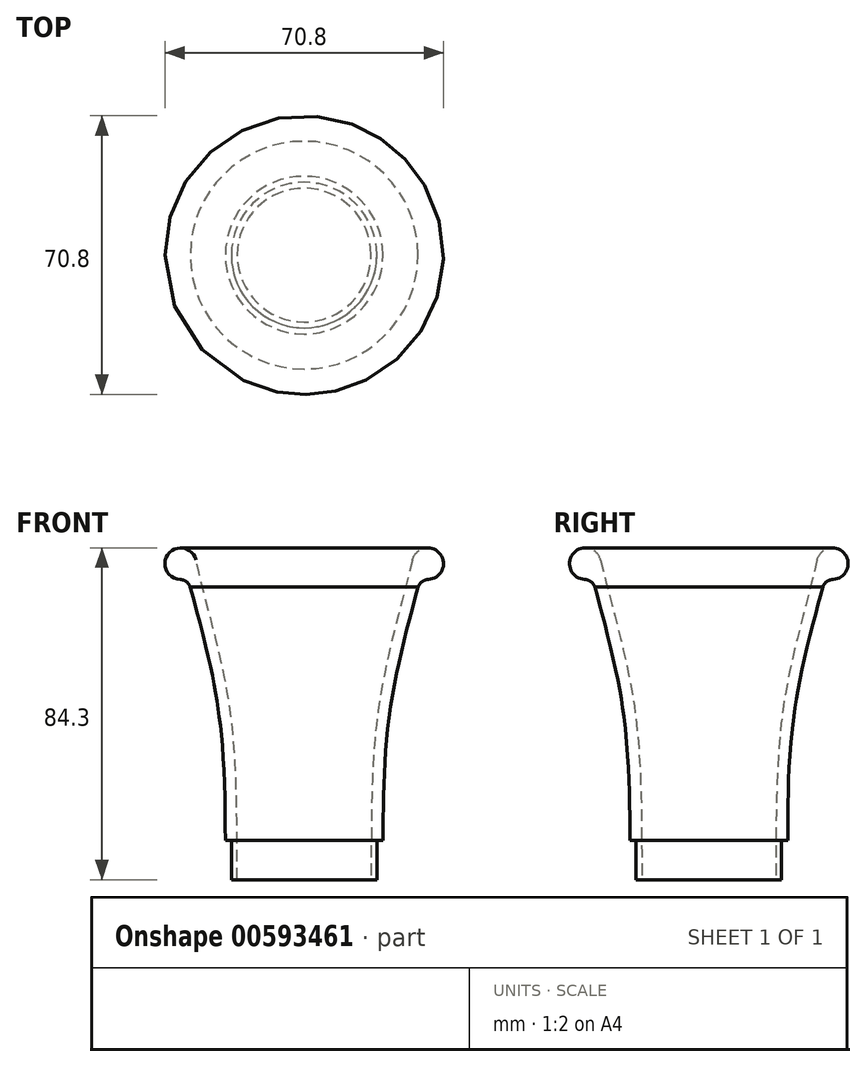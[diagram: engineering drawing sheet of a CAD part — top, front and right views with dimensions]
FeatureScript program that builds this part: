
annotation { "Feature Type Name" : "Feature", "Feature Type Description" : "" }
export const myFeature = defineFeature(function(context is Context, id is Id, definition is map)
    precondition{}
    {
        {
            var Q0;
            Q0=qCreatedBy(makeId("Right.planeOp"),FACE);
            var sketch = newSketch(context, id + "F0", { "sketchPlane" : qUnion([Q0])});
            skFitSpline(sketch, "E0", {"points": [v(-17, 0) * mm, v(-18.93, 44.07) * mm, v(-27.5, 81.2) * mm], "startDerivative": vector(-0.64, 86.47) * mm, "endDerivative": vector(-17.07, 73.05) * mm});
            skLineSegment(sketch, "E1", {"start": v(0, 0) * mm, "end": v(0, 81.2) * mm, "construction": true});
            skLineSegment(sketch, "E2", {"start": v(-27.5, 81.2) * mm, "end": v(0, 81.2) * mm, "construction": true});
            skLineSegment(sketch, "E3", {"start": v(-17, 0) * mm, "end": v(0, 0) * mm, "construction": true});
            skArc(sketch, "E4", {"start": v(-27.5, 81.2) * mm, "mid": v(-34.47, 82.86) * mm, "end": v(-31.59, 76.3) * mm});
            skFitSpline(sketch, "E5.0", {"points": [v(-20, -0.02) * mm, v(-20.03, 3.6) * mm, v(-20.04, 10.81) * mm, v(-20.16, 21.52) * mm, v(-20.53, 30.28) * mm, v(-21.09, 37.13) * mm, v(-21.57, 41.35) * mm, v(-22.05, 44.67) * mm, v(-22.6, 47.97) * mm, v(-23.38, 52.06) * mm, v(-24.46, 56.92) * mm, v(-26.02, 63.33) * mm, v(-28.1, 71.22) * mm, v(-29.7, 77.44) * mm, v(-30.42, 80.52) * mm]});
            skPoint(sketch, "E6.visualSharp", {"position": v(-29.51, 76.77) * mm});
            skArc(sketch, "E6.filletArc", {"start": v(-28.83, 74.05) * mm, "mid": v(-29.84, 75.63) * mm, "end": v(-31.59, 76.3) * mm});
            skLineSegment(sketch, "E7", {"start": v(-20, -0.02) * mm, "end": v(-17, 0) * mm});
            skSolve(sketch);
        }
        {
            var Q0;
            Q0 = qSketchRegion(id + "F0", true);
            var Q1;
            Q1=sQuery(id+"F0.wireOp",EDGE,"E1");
            revolve(context, id + "F1", {"entities" : qUnion([Q0]), "axis" : qUnion([Q1]), "revolveType" : RevolveType.FULL});
        }
        {
            var Q0;
            Q0=qCreatedBy(makeId("Top.planeOp"),FACE);
            var sketch = newSketch(context, id + "F2", { "sketchPlane" : qUnion([Q0])});
            skCircle(sketch, "E8", {"center": v(0, 0) * mm, "radius": 18.5 * mm});
            skCircle(sketch, "E9", {"center": v(0, 0) * mm, "radius": 22.5 * mm});
            skSolve(sketch);
        }
        {
            var Q0;
            Q0=makeQuery(id+"F2.imprint","IMPRINT",FACE,{"disambiguationData":[TD([[makeQuery(id+"F2.imprint","IMPRINT",EDGE,{"derivedFrom":sQuery(id+"F2.wireOp",EDGE,"E8")}),-1.0]])]});
            extrude(context, id + "F3", {"entities" : qUnion([Q0]), "operationType" : NewBodyOperationType.REMOVE, "endBound" : BoundingType.SYMMETRIC, "depth" : 20 * mm, "offsetDistance" : 25 * mm});
        }
    });
